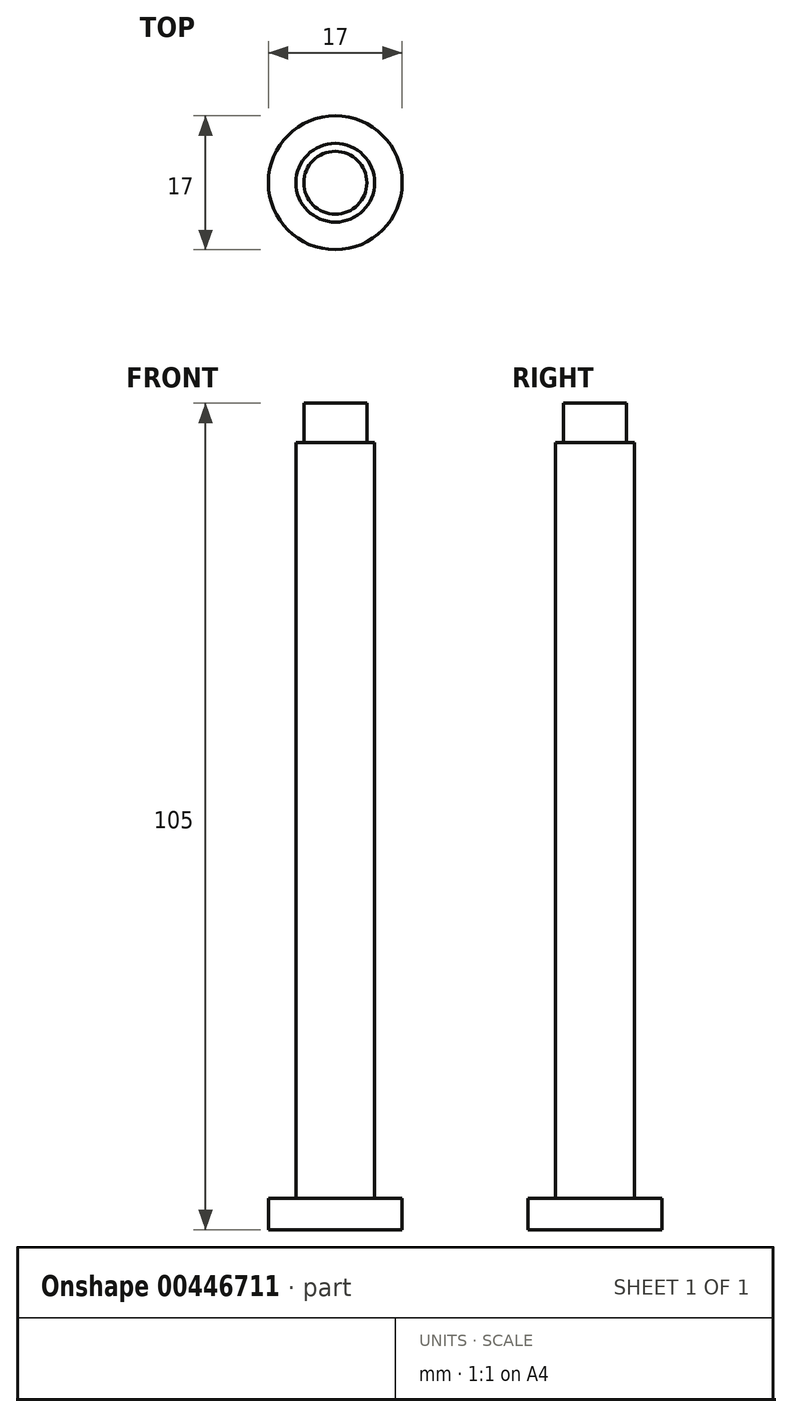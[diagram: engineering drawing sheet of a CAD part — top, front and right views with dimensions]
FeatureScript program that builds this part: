
annotation { "Feature Type Name" : "Feature", "Feature Type Description" : "" }
export const myFeature = defineFeature(function(context is Context, id is Id, definition is map)
    precondition{}
    {
        {
            var Q0;
            Q0=qCreatedBy(makeId("Top.planeOp"),FACE);
            var sketch = newSketch(context, id + "F0", { "sketchPlane" : qUnion([Q0])});
            skCircle(sketch, "E0", {"center": v(0, 0) * mm, "radius": 8.5 * mm});
            skSolve(sketch);
        }
        {
            var Q0;
            Q0=qSketchRegion(id+"F0",true);
            extrude(context, id + "F1", {"entities" : qUnion([Q0]), "depth" : 4 * mm});
        }
        {
            var Q0;
            Q0=qCreatedBy(makeId("Top.planeOp"),FACE);
            var sketch = newSketch(context, id + "F2", { "sketchPlane" : qUnion([Q0])});
            skCircle(sketch, "E1", {"center": v(0, 0) * mm, "radius": 5 * mm});
            skSolve(sketch);
        }
        {
            var Q0;
            Q0=qSketchRegion(id+"F2",true);
            extrude(context, id + "F3", {"entities" : qUnion([Q0]), "operationType" : NewBodyOperationType.ADD, "depth" : 100 * mm});
        }
        {
            var Q0;
            Q0=qCreatedBy(makeId("Right.planeOp"),FACE);
            var sketch = newSketch(context, id + "F4", { "sketchPlane" : qUnion([Q0])});
            skLineSegment(sketch, "E2", {"start": v(0, 105) * mm, "end": v(0, 100) * mm});
            skLineSegment(sketch, "E3", {"start": v(0, 100) * mm, "end": v(4, 100) * mm});
            skLineSegment(sketch, "E4", {"start": v(4, 100) * mm, "end": v(4, 105) * mm});
            skLineSegment(sketch, "E5", {"start": v(4, 105) * mm, "end": v(0, 105) * mm});
            skSolve(sketch);
        }
        {
            var Q0;
            Q0=qSketchRegion(id+"F4",true);
            var Q1;
            Q1=sQuery(id+"F4.wireOp",EDGE,"E2");
            revolve(context, id + "F5", {"operationType" : NewBodyOperationType.ADD, "entities" : qUnion([Q0]), "axis" : qUnion([Q1]), "revolveType" : RevolveType.FULL});
        }
    });
